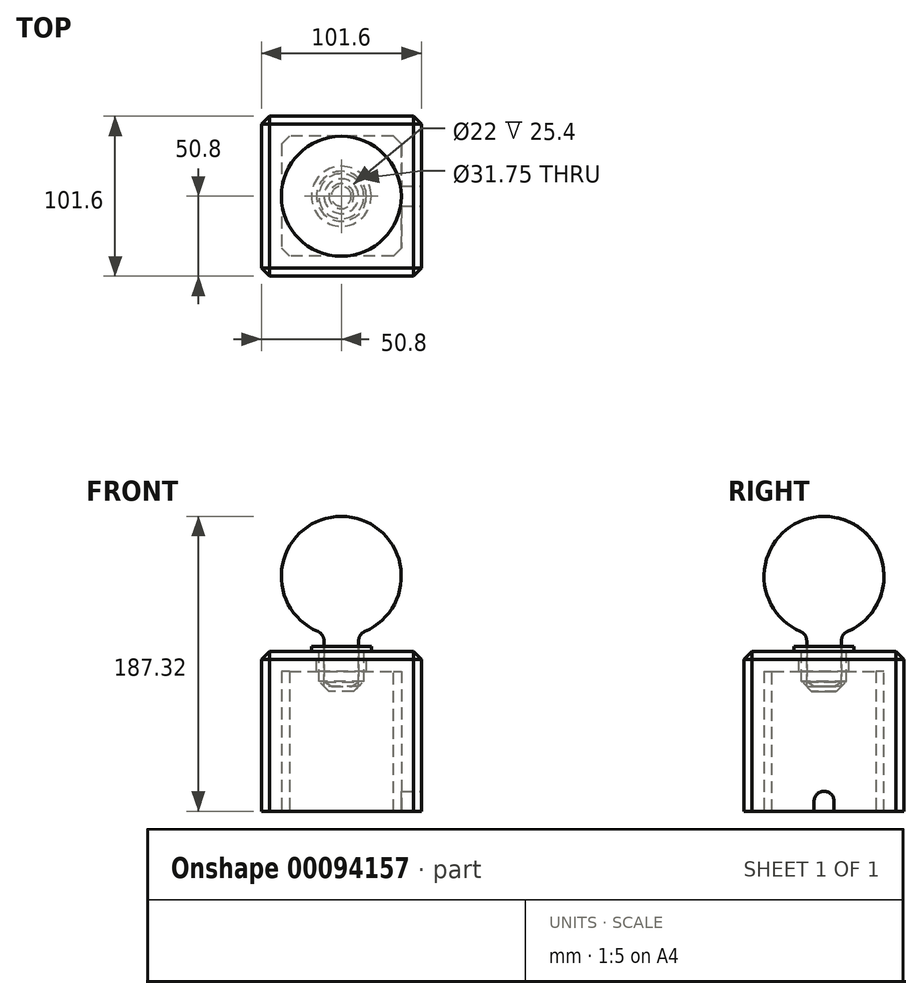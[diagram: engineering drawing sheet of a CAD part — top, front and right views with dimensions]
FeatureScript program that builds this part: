
annotation { "Feature Type Name" : "Feature", "Feature Type Description" : "" }
export const myFeature = defineFeature(function(context is Context, id is Id, definition is map)
    precondition{}
    {
        {
            var Q0;
            Q0=qCreatedBy(makeId("Top.planeOp"),FACE);
            var sketch = newSketch(context, id + "F0", { "sketchPlane" : qUnion([Q0])});
            skLineSegment(sketch, "E0.bottom", {"start": v(50.8, 50.8) * mm, "end": v(-50.8, 50.8) * mm});
            skLineSegment(sketch, "E0.top", {"start": v(50.8, -50.8) * mm, "end": v(-50.8, -50.8) * mm});
            skLineSegment(sketch, "E0.left", {"start": v(50.8, 50.8) * mm, "end": v(50.8, -50.8) * mm});
            skLineSegment(sketch, "E0.right", {"start": v(-50.8, 50.8) * mm, "end": v(-50.8, -50.8) * mm});
            skPoint(sketch, "E0.middle", {"position": v(0, 0) * mm});
            skLineSegment(sketch, "E1.bottom", {"start": v(38.1, 38.1) * mm, "end": v(-38.1, 38.1) * mm});
            skLineSegment(sketch, "E1.top", {"start": v(38.1, -38.1) * mm, "end": v(-38.1, -38.1) * mm});
            skLineSegment(sketch, "E1.left", {"start": v(38.1, 38.1) * mm, "end": v(38.1, -38.1) * mm});
            skLineSegment(sketch, "E1.right", {"start": v(-38.1, 38.1) * mm, "end": v(-38.1, -38.1) * mm});
            skSolve(sketch);
        }
        {
            var Q0;
            Q0=makeQuery(id+"F0.imprint","IMPRINT",FACE,{"disambiguationData":[TD([[makeQuery(id+"F0.imprint","IMPRINT",EDGE,{"derivedFrom":sQuery(id+"F0.wireOp",EDGE,"E0.bottom")}),1.0]])]});
            extrude(context, id + "F1", {"entities" : qUnion([Q0]), "oppositeDirection" : true, "depth" : 101.6 * mm});
        }
        {
            var Q0;
            Q0=qCreatedBy(makeId("Top.planeOp"),FACE);
            var sketch = newSketch(context, id + "F2", { "sketchPlane" : qUnion([Q0])});
            skLineSegment(sketch, "E2.bottom", {"start": v(-38.1, -38.1) * mm, "end": v(38.1, -38.1) * mm});
            skLineSegment(sketch, "E2.top", {"start": v(-38.1, 38.1) * mm, "end": v(38.1, 38.1) * mm});
            skLineSegment(sketch, "E2.left", {"start": v(-38.1, -38.1) * mm, "end": v(-38.1, 38.1) * mm});
            skLineSegment(sketch, "E2.right", {"start": v(38.1, -38.1) * mm, "end": v(38.1, 38.1) * mm});
            skCircle(sketch, "E3", {"center": v(0, 0) * mm, "radius": 15.88 * mm});
            skSolve(sketch);
        }
        {
            var Q0;
            Q0 = qSketchRegion(id + "F2", true);
            extrude(context, id + "F3", {"entities" : qUnion([Q0]), "operationType" : NewBodyOperationType.ADD, "oppositeDirection" : true, "depth" : 12.7 * mm});
        }
        {
            var Q0;
            Q0=makeQuery(id+"F1.opExtrude","SWEPT_FACE",FACE,{"disambiguationData":[OSD([sQuery(id+"F0.wireOp",EDGE,"E0.left")])]});
            var sketch = newSketch(context, id + "F4", { "sketchPlane" : qUnion([Q0])});
            skLineSegment(sketch, "E4.bottom", {"start": v(-6.35, -101.6) * mm, "end": v(6.35, -101.6) * mm});
            skLineSegment(sketch, "E4.left", {"start": v(-6.35, -101.6) * mm, "end": v(-6.35, -95.25) * mm});
            skLineSegment(sketch, "E4.right", {"start": v(6.35, -101.6) * mm, "end": v(6.35, -95.25) * mm});
            skArc(sketch, "E5", {"start": v(6.35, -95.25) * mm, "mid": v(0, -88.9) * mm, "end": v(-6.35, -95.25) * mm});
            skPoint(sketch, "E6", {"position": v(0, -101.6) * mm});
            skSolve(sketch);
        }
        {
            var Q0;
            Q0 = qSketchRegion(id + "F4", true);
            extrude(context, id + "F5", {"entities" : qUnion([Q0]), "operationType" : NewBodyOperationType.REMOVE, "endBound" : BoundingType.UP_TO_NEXT, "oppositeDirection" : true, "depth" : 25.4 * mm});
        }
        {
            var Q0;
            Q0=qCreatedBy(makeId("Right.planeOp"),FACE);
            var sketch = newSketch(context, id + "F6", { "sketchPlane" : qUnion([Q0])});
            skLineSegment(sketch, "E7", {"start": v(0, 0) * mm, "end": v(0, -25.4) * mm});
            skLineSegment(sketch, "E8", {"start": v(0, -25.4) * mm, "end": v(7.94, -25.4) * mm});
            skLineSegment(sketch, "E9", {"start": v(7.94, -25.4) * mm, "end": v(14.29, -19.05) * mm});
            skLineSegment(sketch, "E10", {"start": v(14.29, -19.05) * mm, "end": v(14.29, 0) * mm});
            skLineSegment(sketch, "E11", {"start": v(14.29, 0) * mm, "end": v(19.05, 0) * mm});
            skLineSegment(sketch, "E12", {"start": v(19.05, 0) * mm, "end": v(19.05, 3.17) * mm});
            skLineSegment(sketch, "E13", {"start": v(19.05, 3.18) * mm, "end": v(11, 3.17) * mm});
            skLineSegment(sketch, "E14", {"start": v(11, 3.18) * mm, "end": v(11, -22.23) * mm});
            skLineSegment(sketch, "E15", {"start": v(11, -22.23) * mm, "end": v(0, -22.23) * mm});
            skPoint(sketch, "E16", {"position": v(15.88, 0) * mm});
            skSolve(sketch);
        }
        {
            var Q0;
            {var subQ0=sQuery(id+"F6.wireOp",EDGE,"E8");Q0=makeQuery(id+"F6.imprint","IMPRINT",FACE,{"disambiguationData":[TD([[makeQuery(id+"F6.imprint","IMPRINT",EDGE,{"derivedFrom":subQ0}),1.0]])]});}
            var Q1;
            Q1=sQuery(id+"F6.wireOp",EDGE,"E7");
            revolve(context, id + "F7", {"entities" : qUnion([Q0]), "axis" : qUnion([Q1]), "revolveType" : RevolveType.FULL});
        }
        {
            var Q0;
            Q0=qCreatedBy(makeId("Right.planeOp"),FACE);
            var sketch = newSketch(context, id + "F8", { "sketchPlane" : qUnion([Q0])});
            skArc(sketch, "E17", {"start": v(14.87, 12.55) * mm, "mid": v(37.34, 55.21) * mm, "end": v(0, 85.73) * mm});
            skLineSegment(sketch, "E18", {"start": v(0, 9.52) * mm, "end": v(0, -22.23) * mm});
            skLineSegment(sketch, "E19", {"start": v(11, -19.54) * mm, "end": v(11, 6.7) * mm});
            skLineSegment(sketch, "E20", {"start": v(0, -22.23) * mm, "end": v(6.35, -22.23) * mm});
            skLineSegment(sketch, "E21", {"start": v(6.35, -22.23) * mm, "end": v(11, -19.54) * mm});
            skLineSegment(sketch, "E22", {"start": v(0, 9.52) * mm, "end": v(0, 85.72) * mm});
            skPoint(sketch, "E23.visualSharp", {"position": v(11, 11.15) * mm});
            skArc(sketch, "E23.filletArc", {"start": v(14.87, 12.55) * mm, "mid": v(12.06, 10.2) * mm, "end": v(11, 6.7) * mm});
            skSolve(sketch);
        }
        {
            var Q0;
            Q0 = qSketchRegion(id + "F8", true);
            var Q1;
            Q1=sQuery(id+"F8.wireOp",EDGE,"E22");
            revolve(context, id + "F9", {"entities" : qUnion([Q0]), "axis" : qUnion([Q1]), "revolveType" : RevolveType.FULL});
        }
        {
            var Q0;
            Q0=makeQuery(id+"F1.opExtrude","CAP_EDGE",EDGE,{"disambiguationData":[OSD([sQuery(id+"F0.wireOp",EDGE,"E0.right")])],"isStart":true});
            var Q1;
            Q1=makeQuery(id+"F1.opExtrude","CAP_EDGE",EDGE,{"disambiguationData":[OSD([sQuery(id+"F0.wireOp",EDGE,"E0.top")])],"isStart":true});
            var Q2;
            Q2=makeQuery(id+"F1.opExtrude","CAP_EDGE",EDGE,{"disambiguationData":[OSD([sQuery(id+"F0.wireOp",EDGE,"E0.left")])],"isStart":true});
            var Q3;
            Q3=makeQuery(id+"F1.opExtrude","CAP_EDGE",EDGE,{"disambiguationData":[OSD([sQuery(id+"F0.wireOp",EDGE,"E0.bottom")])],"isStart":true});
            var Q4;
            Q4=makeQuery(id+"F1.opExtrude","SWEPT_EDGE",EDGE,{"disambiguationData":[OSD([sQuery(id+"F0.wireOp",EDGE,"E0.top"),sQuery(id+"F0.wireOp",EDGE,"E0.right")])]});
            var Q5;
            Q5=makeQuery(id+"F1.opExtrude","SWEPT_EDGE",EDGE,{"disambiguationData":[OSD([sQuery(id+"F0.wireOp",EDGE,"E0.top"),sQuery(id+"F0.wireOp",EDGE,"E0.left")])]});
            var Q6;
            Q6=makeQuery(id+"F1.opExtrude","SWEPT_EDGE",EDGE,{"disambiguationData":[OSD([sQuery(id+"F0.wireOp",EDGE,"E0.bottom"),sQuery(id+"F0.wireOp",EDGE,"E0.right")])]});
            var Q7;
            Q7=makeQuery(id+"F1.opExtrude","SWEPT_EDGE",EDGE,{"disambiguationData":[OSD([sQuery(id+"F0.wireOp",EDGE,"E0.bottom"),sQuery(id+"F0.wireOp",EDGE,"E0.left")])]});
            var Q8;
            Q8=makeQuery(id+"F1.opExtrude","SWEPT_EDGE",EDGE,{"disambiguationData":[OSD([sQuery(id+"F0.wireOp",EDGE,"E1.top"),sQuery(id+"F0.wireOp",EDGE,"E1.left")])]});
            var Q9;
            Q9=makeQuery(id+"F1.opExtrude","SWEPT_EDGE",EDGE,{"disambiguationData":[OSD([sQuery(id+"F0.wireOp",EDGE,"E1.top"),sQuery(id+"F0.wireOp",EDGE,"E1.right")])]});
            var Q10;
            Q10=makeQuery(id+"F1.opExtrude","SWEPT_EDGE",EDGE,{"disambiguationData":[OSD([sQuery(id+"F0.wireOp",EDGE,"E1.bottom"),sQuery(id+"F0.wireOp",EDGE,"E1.left")])]});
            var Q11;
            Q11=makeQuery(id+"F1.opExtrude","SWEPT_EDGE",EDGE,{"disambiguationData":[OSD([sQuery(id+"F0.wireOp",EDGE,"E1.bottom"),sQuery(id+"F0.wireOp",EDGE,"E1.right")])]});
            chamfer(context, id + "F10", {"entities" : qUnion([Q0, Q1, Q2, Q3, Q4, Q5, Q6, Q7, Q8, Q9, Q10, Q11]), "width" : 5.08 * mm, "tangentPropagation" : true});
        }
    });
